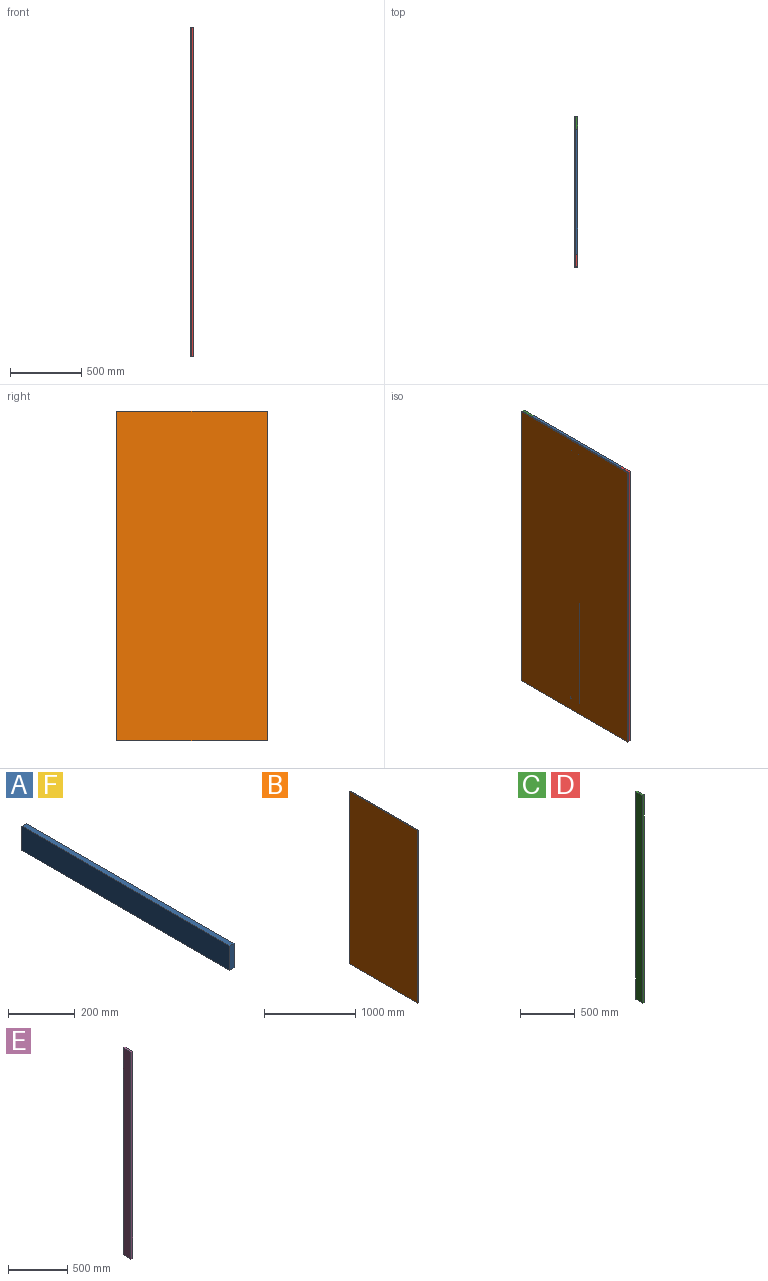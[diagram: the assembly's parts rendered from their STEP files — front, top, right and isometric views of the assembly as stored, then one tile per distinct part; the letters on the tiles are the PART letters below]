
ASSEMBLY  parts=6 mates=5
PART A: 6 faces, bbox 19.1x876.3x88.9 mm
  f0: plane 876.3x19.05mm, normal (0,0,1), area 16693.5mm2, adj f1,f3,f4,f5
  f1: plane 876.3x88.9mm, normal (-1,0,0), area 77903.1mm2, adj f0,f2,f4,f5
  f2: plane 876.3x19.05mm, normal (0,0,-1), area 16693.5mm2, adj f1,f3,f4,f5
  f3: plane 876.3x88.9mm, normal (1,0,0), area 77903.1mm2, adj f0,f2,f4,f5
  f4: plane 88.9x19.05mm, normal (0,1,0), area 1693.5mm2, adj f0,f1,f2,f3
  f5: plane 88.9x19.05mm, normal (0,-1,0), area 1693.5mm2, adj f0,f1,f2,f3
PART B: 6 faces, bbox 6.4x1054.1x2311.4 mm
  f0: plane 1054.1x6.35mm, normal (0,0,1), area 6693.5mm2, adj f1,f3,f4,f5
  f1: plane 2311.4x6.35mm, normal (0,-1,0), area 14677.4mm2, adj f0,f2,f4,f5
  f2: plane 1054.1x6.35mm, normal (0,0,-1), area 6693.5mm2, adj f1,f3,f4,f5
  f3: plane 2311.4x6.35mm, normal (0,1,0), area 14677.4mm2, adj f0,f2,f4,f5
  f4: plane 2311.4x1054.1mm, normal (1,0,0), area 2436446.7mm2, adj f0,f1,f2,f3
  f5: plane 2311.4x1054.1mm, normal (-1,0,0), area 2436446.7mm2, adj f0,f1,f2,f3
PART C: 6 faces, bbox 19.1x88.9x2311.4 mm
  f0: plane 2311.4x88.9mm, normal (-1,0,0), area 205483.5mm2, adj f1,f3,f4,f5
  f1: plane 2311.4x19.05mm, normal (0,-1,0), area 44032.2mm2, adj f0,f2,f4,f5
  f2: plane 2311.4x88.9mm, normal (1,0,0), area 205483.5mm2, adj f1,f3,f4,f5
  f3: plane 2311.4x19.05mm, normal (0,1,0), area 44032.2mm2, adj f0,f2,f4,f5
  f4: plane 88.9x19.05mm, normal (0,0,-1), area 1693.5mm2, adj f0,f1,f2,f3
  f5: plane 88.9x19.05mm, normal (0,0,1), area 1693.5mm2, adj f0,f1,f2,f3
PART D: same geometry as C
PART E: 6 faces, bbox 19.1x88.9x2133.6 mm
  f0: plane 2133.6x88.9mm, normal (-1,0,0), area 189677mm2, adj f1,f3,f4,f5
  f1: plane 2133.6x19.05mm, normal (0,-1,0), area 40645.1mm2, adj f0,f2,f4,f5
  f2: plane 2133.6x88.9mm, normal (1,0,0), area 189677mm2, adj f1,f3,f4,f5
  f3: plane 2133.6x19.05mm, normal (0,1,0), area 40645.1mm2, adj f0,f2,f4,f5
  f4: plane 88.9x19.05mm, normal (0,0,-1), area 1693.5mm2, adj f0,f1,f2,f3
  f5: plane 88.9x19.05mm, normal (0,0,1), area 1693.5mm2, adj f0,f1,f2,f3
PART F: same geometry as A
PLACE A t=(-686.26,-361.04,1761.47)mm
PLACE B t=(-692.61,557.28,-415.69)mm
PLACE C t=(-686.26,551.27,1832.03)mm
PLACE D t=(-686.26,-413.93,1832.03)mm
PLACE E t=(-686.26,62.36,1743.13)mm
PLACE F t=(-686.26,-361.04,-461.03)mm
MATE fastened F.f1 <-> B.f4  axis (-1,0,0) through (-686.26,77.11,-479.37)mm
MATE fastened A.f1 <-> B.f4  axis (-1,0,0) through (-686.26,77.11,1832.03)mm
MATE fastened D.f0 <-> B.f4  axis (-1,0,0) through (-686.26,-449.94,676.33)mm
MATE fastened C.f0 <-> B.f4  axis (-1,0,0) through (-686.26,604.16,676.33)mm
MATE fastened E.f0 <-> B.f4  axis (-1,0,0) through (-686.26,77.11,676.33)mm
